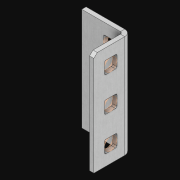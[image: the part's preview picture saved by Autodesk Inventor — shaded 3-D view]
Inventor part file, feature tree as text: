
AUTODESK INVENTOR PART (.ipt)
format: ipt  version: 2021 (Build 250183000, 183)  size: 1,034,752 bytes
history: native  units: in
note: dims shown in document units (in); Inventor stores cm internally (conversion verified against a paired STEP export)
features: extrude x8, other x6, sketch x4, pattern_linear x2, sheet_metal_op x1
ambient origin geometry x8: Origin, YZ Plane, XZ Plane, XY Plane, X Axis, Y Axis, Z Axis, Center Point
bodies: Solid1 (feature_tree)
feature tree (21):
  pattern_linear  "Rectangular Pattern1"  Spacing1=0.5in  [1 undecoded]
  pattern_linear  "Rectangular Pattern3"  Count1=3  [1 undecoded]
  extrude  "Extrusion1"  Depth=0.5in
  extrude  "Extrusion2"  Depth=0.841in
  sketch  "Sketch1"  dims[d0=0.182in]
  other  "Srf1"
  sketch  "Sketch3"  dims[d1=0.063in d2=0.0in]
  other  "Srf3"
  other  "Srf4"
  other  "Srf5"
  other  "Srf142"
  other  "Srf143"
  sketch  "Sketch4"  dims[d6=0.182in]
  sketch  "Sketch5"  dims[d7=0.063in d8=0.0in d11=0.5in d12=0.3937in d14=0.5in d18=1.1811in d20=0.5in d21=16.0in d22=0.0in d23=0.841in d24=0.0in]
  sheet_metal_op  "Fold1"
  extrude  "ExtrusionSrf1"  TaperAngle=0.0deg  [1 undecoded]
  extrude  "ExtrusionSrf3"  Depth=0.841in TaperAngle=0.0deg
  extrude  "ExtrusionSrf4"  [1 undecoded]
  extrude  "ExtrusionSrf5"  [1 undecoded]
  extrude  "ExtrusionSrf142"  [1 undecoded]
  extrude  "ExtrusionSrf143"  [1 undecoded]
note: 7 required parameter values undecoded (feature->parameter linkage not recoverable at this tier; creation-order binding heuristic only, values carry confidence <= 0.55)
